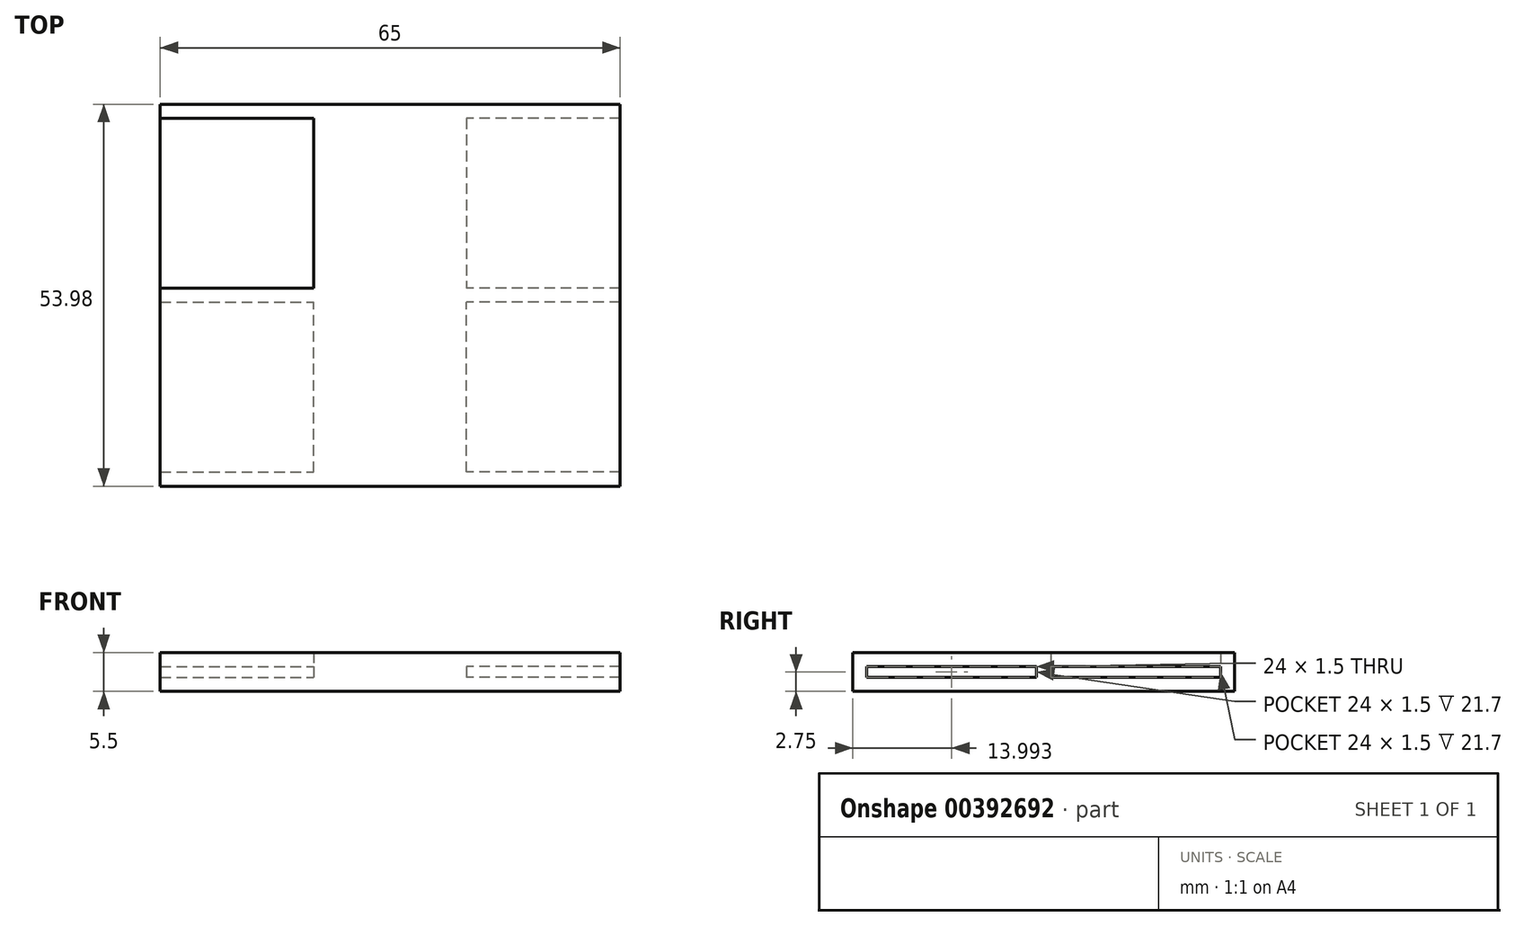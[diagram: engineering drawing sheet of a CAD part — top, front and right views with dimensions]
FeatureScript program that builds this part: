
annotation { "Feature Type Name" : "Feature", "Feature Type Description" : "" }
export const myFeature = defineFeature(function(context is Context, id is Id, definition is map)
    precondition{}
    {
        {
            assignVariable(context, id + "F0", {"name" : "SDThickness", "anyValue" : 1.5});
        }
        {
            var Q0;
            Q0=qCreatedBy(makeId("Top.planeOp"),FACE);
            var sketch = newSketch(context, id + "F1", { "sketchPlane" : qUnion([Q0])});
            skLineSegment(sketch, "E0.bottom", {"start": v(-42.8, 26.99) * mm, "end": v(42.8, 26.99) * mm});
            skLineSegment(sketch, "E0.top", {"start": v(-42.8, -26.99) * mm, "end": v(42.8, -26.99) * mm});
            skLineSegment(sketch, "E0.left", {"start": v(-42.8, 26.99) * mm, "end": v(-42.8, -26.99) * mm});
            skLineSegment(sketch, "E0.right", {"start": v(42.8, 26.99) * mm, "end": v(42.8, -26.99) * mm});
            skPoint(sketch, "E0.middle", {"position": v(0, 0) * mm});
            skSolve(sketch);
        }
        {
            var Q0;
            Q0=qCreatedBy(makeId("Top.planeOp"),FACE);
            var sketch = newSketch(context, id + "F2", { "sketchPlane" : qUnion([Q0])});
            skLineSegment(sketch, "E1.0", {"start": v(-42.8, 26.99) * mm, "end": v(42.8, 26.99) * mm});
            skLineSegment(sketch, "E2.0", {"start": v(-42.8, 26.99) * mm, "end": v(-42.8, -26.99) * mm});
            skLineSegment(sketch, "E3.0", {"start": v(-42.8, -26.99) * mm, "end": v(42.8, -26.99) * mm});
            skLineSegment(sketch, "E4.0", {"start": v(42.8, 26.99) * mm, "end": v(42.8, -26.99) * mm});
            skLineSegment(sketch, "E5.bottom", {"start": v(-42.8, 25) * mm, "end": v(-10.8, 25) * mm});
            skLineSegment(sketch, "E5.top", {"start": v(-42.8, 1) * mm, "end": v(-10.8, 1) * mm});
            skLineSegment(sketch, "E5.left", {"start": v(-42.8, 25) * mm, "end": v(-42.8, 1) * mm});
            skLineSegment(sketch, "E5.right", {"start": v(-10.8, 25) * mm, "end": v(-10.8, 1) * mm});
            skLineSegment(sketch, "E6.bottom", {"start": v(42.8, 25) * mm, "end": v(10.8, 25) * mm});
            skLineSegment(sketch, "E6.top", {"start": v(42.8, 1) * mm, "end": v(10.8, 1) * mm});
            skLineSegment(sketch, "E6.left", {"start": v(42.8, 25) * mm, "end": v(42.8, 1) * mm});
            skLineSegment(sketch, "E6.right", {"start": v(10.8, 25) * mm, "end": v(10.8, 1) * mm});
            skLineSegment(sketch, "E7.bottom", {"start": v(42.8, -25) * mm, "end": v(10.8, -25) * mm});
            skLineSegment(sketch, "E7.top", {"start": v(42.8, -1) * mm, "end": v(10.8, -1) * mm});
            skLineSegment(sketch, "E7.left", {"start": v(42.8, -25) * mm, "end": v(42.8, -1) * mm});
            skLineSegment(sketch, "E7.right", {"start": v(10.8, -25) * mm, "end": v(10.8, -1) * mm});
            skLineSegment(sketch, "E8.bottom", {"start": v(-42.8, -25) * mm, "end": v(-10.8, -25) * mm});
            skLineSegment(sketch, "E8.top", {"start": v(-42.8, -1) * mm, "end": v(-10.8, -1) * mm});
            skLineSegment(sketch, "E8.left", {"start": v(-42.8, -25) * mm, "end": v(-42.8, -1) * mm});
            skLineSegment(sketch, "E8.right", {"start": v(-10.8, -25) * mm, "end": v(-10.8, -1) * mm});
            skLineSegment(sketch, "E9", {"start": v(-26.8, 25) * mm, "end": v(-26.8, 26.99) * mm, "construction": true});
            skLineSegment(sketch, "E10", {"start": v(-26.8, 1) * mm, "end": v(-26.8, -1) * mm, "construction": true});
            skLineSegment(sketch, "E11", {"start": v(-26.8, -25) * mm, "end": v(-26.8, -26.99) * mm, "construction": true});
            skLineSegment(sketch, "E12", {"start": v(26.8, 25) * mm, "end": v(26.8, 26.99) * mm, "construction": true});
            skLineSegment(sketch, "E13", {"start": v(26.8, 1) * mm, "end": v(26.8, -1) * mm, "construction": true});
            skLineSegment(sketch, "E14", {"start": v(26.8, -25) * mm, "end": v(26.8, -26.99) * mm, "construction": true});
            skLineSegment(sketch, "E15", {"start": v(32.5, 27) * mm, "end": v(32.5, -26.99) * mm});
            skLineSegment(sketch, "E16", {"start": v(-32.5, 26.99) * mm, "end": v(-32.5, -26.99) * mm});
            skLineSegment(sketch, "E17", {"start": v(32.5, 27) * mm, "end": v(-32.5, -27) * mm, "construction": true});
            skLineSegment(sketch, "E18", {"start": v(-32.5, 27) * mm, "end": v(32.5, -27) * mm, "construction": true});
            skSolve(sketch);
        }
        {
            var Q0;
            {var subQ11=sQuery(id+"F2.wireOp",EDGE,"E5.right");Q0=makeQuery(id+"F2.imprint","IMPRINT",FACE,{"disambiguationData":[TD([[makeQuery(id+"F2.imprint","IMPRINT",EDGE,{"derivedFrom":subQ11}),1.0]])]});}
            var Q1;
            {var subQ0=sQuery(id+"F2.wireOp",EDGE,"E6.right");Q1=makeQuery(id+"F2.imprint","IMPRINT",FACE,{"disambiguationData":[TD([[makeQuery(id+"F2.imprint","IMPRINT",EDGE,{"derivedFrom":subQ0}),1.0]])]});}
            var Q2;
            {var subQ0=sQuery(id+"F2.wireOp",EDGE,"E8.right");Q2=makeQuery(id+"F2.imprint","IMPRINT",FACE,{"disambiguationData":[TD([[makeQuery(id+"F2.imprint","IMPRINT",EDGE,{"derivedFrom":subQ0}),1.0]])]});}
            var Q3;
            {var subQ0=sQuery(id+"F2.wireOp",EDGE,"E5.right");Q3=makeQuery(id+"F2.imprint","IMPRINT",FACE,{"disambiguationData":[TD([[makeQuery(id+"F2.imprint","IMPRINT",EDGE,{"derivedFrom":subQ0}),-1.0]])]});}
            var Q4;
            {var subQ0=sQuery(id+"F2.wireOp",EDGE,"E7.right");Q4=makeQuery(id+"F2.imprint","IMPRINT",FACE,{"disambiguationData":[TD([[makeQuery(id+"F2.imprint","IMPRINT",EDGE,{"derivedFrom":subQ0}),-1.0]])]});}
            extrude(context, id + "F3", {"entities" : qUnion([Q0, Q1, Q2, Q3, Q4]), "depth" : -2 * mm});
        }
        {
            var Q0;
            {var subQ11=sQuery(id+"F2.wireOp",EDGE,"E5.right");Q0=makeQuery(id+"F2.imprint","IMPRINT",FACE,{"disambiguationData":[TD([[makeQuery(id+"F2.imprint","IMPRINT",EDGE,{"derivedFrom":subQ11}),1.0]])]});}
            extrude(context, id + "F4", {"entities" : qUnion([Q0]), "operationType" : NewBodyOperationType.ADD, "depth" : (getVariable(context, 'SDThickness')) * mm});
        }
        {
            var Q0;
            Q0=makeQuery(id+"F4.opExtrude","CAP_FACE",FACE,{"disambiguationData":[OSD([sQuery(id+"F2.wireOp",EDGE,"E1.0"),sQuery(id+"F2.wireOp",EDGE,"E3.0"),sQuery(id+"F2.wireOp",EDGE,"E5.bottom"),sQuery(id+"F2.wireOp",EDGE,"E5.top"),sQuery(id+"F2.wireOp",EDGE,"E5.right"),sQuery(id+"F2.wireOp",EDGE,"E6.bottom"),sQuery(id+"F2.wireOp",EDGE,"E6.top"),sQuery(id+"F2.wireOp",EDGE,"E6.right"),sQuery(id+"F2.wireOp",EDGE,"E7.bottom"),sQuery(id+"F2.wireOp",EDGE,"E7.top"),sQuery(id+"F2.wireOp",EDGE,"E7.right"),sQuery(id+"F2.wireOp",EDGE,"E8.bottom"),sQuery(id+"F2.wireOp",EDGE,"E8.top"),sQuery(id+"F2.wireOp",EDGE,"E8.right"),sQuery(id+"F2.wireOp",EDGE,"E15"),sQuery(id+"F2.wireOp",EDGE,"E16")])],"isStart":false});
            var sketch = newSketch(context, id + "F5", { "sketchPlane" : qUnion([Q0])});
            skLineSegment(sketch, "E19.0.0", {"start": v(10.8, -1) * mm, "end": v(32.5, -1) * mm});
            skLineSegment(sketch, "E19.0.1", {"start": v(32.5, -1) * mm, "end": v(32.5, 1) * mm});
            skLineSegment(sketch, "E19.0.2", {"start": v(32.5, 1) * mm, "end": v(10.8, 1) * mm});
            skLineSegment(sketch, "E19.0.3", {"start": v(10.8, 1) * mm, "end": v(10.8, 25) * mm});
            skLineSegment(sketch, "E19.0.4", {"start": v(10.8, 25) * mm, "end": v(32.5, 25) * mm});
            skLineSegment(sketch, "E19.0.5", {"start": v(32.5, 25) * mm, "end": v(32.5, 26.99) * mm});
            skLineSegment(sketch, "E19.0.6", {"start": v(32.5, 26.99) * mm, "end": v(-32.5, 26.99) * mm});
            skLineSegment(sketch, "E19.0.7", {"start": v(-32.5, 26.99) * mm, "end": v(-32.5, 25) * mm});
            skLineSegment(sketch, "E19.0.8", {"start": v(-32.5, 25) * mm, "end": v(-10.8, 25) * mm});
            skLineSegment(sketch, "E19.0.9", {"start": v(-10.8, 25) * mm, "end": v(-10.8, 1) * mm});
            skLineSegment(sketch, "E19.0.10", {"start": v(-10.8, 1) * mm, "end": v(-32.5, 1) * mm});
            skLineSegment(sketch, "E19.0.11", {"start": v(-32.5, 1) * mm, "end": v(-32.5, -1) * mm});
            skLineSegment(sketch, "E19.0.12", {"start": v(-32.5, -1) * mm, "end": v(-10.8, -1) * mm});
            skLineSegment(sketch, "E19.0.13", {"start": v(-10.8, -1) * mm, "end": v(-10.8, -25) * mm});
            skLineSegment(sketch, "E19.0.14", {"start": v(-10.8, -25) * mm, "end": v(-32.5, -25) * mm});
            skLineSegment(sketch, "E19.0.15", {"start": v(-32.5, -25) * mm, "end": v(-32.5, -26.99) * mm});
            skLineSegment(sketch, "E19.0.16", {"start": v(-32.5, -26.99) * mm, "end": v(32.5, -26.99) * mm});
            skLineSegment(sketch, "E19.0.17", {"start": v(32.5, -26.99) * mm, "end": v(32.5, -25) * mm});
            skLineSegment(sketch, "E19.0.18", {"start": v(32.5, -25) * mm, "end": v(10.8, -25) * mm});
            skLineSegment(sketch, "E19.0.19", {"start": v(10.8, -25) * mm, "end": v(10.8, -1) * mm});
            skLineSegment(sketch, "E20.0.0", {"start": v(-10.8, 25) * mm, "end": v(-32.5, 25) * mm});
            skLineSegment(sketch, "E20.0.1", {"start": v(-32.5, 25) * mm, "end": v(-32.5, 1) * mm});
            skLineSegment(sketch, "E20.0.2", {"start": v(-32.5, 1) * mm, "end": v(-10.8, 1) * mm});
            skLineSegment(sketch, "E20.0.3", {"start": v(-10.8, 1) * mm, "end": v(-10.8, 25) * mm});
            skLineSegment(sketch, "E21.0.0", {"start": v(-32.5, -1) * mm, "end": v(-32.5, -25) * mm});
            skLineSegment(sketch, "E21.0.1", {"start": v(-32.5, -25) * mm, "end": v(-10.8, -25) * mm});
            skLineSegment(sketch, "E21.0.2", {"start": v(-10.8, -25) * mm, "end": v(-10.8, -1) * mm});
            skLineSegment(sketch, "E21.0.3", {"start": v(-10.8, -1) * mm, "end": v(-32.5, -1) * mm});
            skLineSegment(sketch, "E22.0.0", {"start": v(32.5, -25) * mm, "end": v(32.5, -1) * mm});
            skLineSegment(sketch, "E22.0.1", {"start": v(32.5, -1) * mm, "end": v(10.8, -1) * mm});
            skLineSegment(sketch, "E22.0.2", {"start": v(10.8, -1) * mm, "end": v(10.8, -25) * mm});
            skLineSegment(sketch, "E22.0.3", {"start": v(10.8, -25) * mm, "end": v(32.5, -25) * mm});
            skLineSegment(sketch, "E23.0.0", {"start": v(32.5, 1) * mm, "end": v(32.5, 25) * mm});
            skLineSegment(sketch, "E23.0.1", {"start": v(32.5, 25) * mm, "end": v(10.8, 25) * mm});
            skLineSegment(sketch, "E23.0.2", {"start": v(10.8, 25) * mm, "end": v(10.8, 1) * mm});
            skLineSegment(sketch, "E23.0.3", {"start": v(10.8, 1) * mm, "end": v(32.5, 1) * mm});
            skSolve(sketch);
        }
        {
            var Q0;
            Q0=makeQuery(id+"F5.imprint","IMPRINT",FACE,{"disambiguationData":[TD([[makeQuery(id+"F5.imprint","IMPRINT",EDGE,{"derivedFrom":sQuery(id+"F5.wireOp",EDGE,"E19.0.1")}),-1.0]])]});
            var Q1;
            Q1=makeQuery(id+"F5.imprint","IMPRINT",FACE,{"disambiguationData":[TD([[makeQuery(id+"F5.imprint","IMPRINT",EDGE,{"derivedFrom":sQuery(id+"F5.wireOp",EDGE,"E20.0.0")}),-1.0]])]});
            var Q2;
            Q2=makeQuery(id+"F5.imprint","IMPRINT",FACE,{"disambiguationData":[TD([[makeQuery(id+"F5.imprint","IMPRINT",EDGE,{"derivedFrom":sQuery(id+"F5.wireOp",EDGE,"E21.0.0")}),1.0]])]});
            var Q3;
            Q3=makeQuery(id+"F5.imprint","IMPRINT",FACE,{"disambiguationData":[TD([[makeQuery(id+"F5.imprint","IMPRINT",EDGE,{"derivedFrom":sQuery(id+"F5.wireOp",EDGE,"E23.0.0")}),1.0]])]});
            var Q4;
            Q4=makeQuery(id+"F5.imprint","IMPRINT",FACE,{"disambiguationData":[TD([[makeQuery(id+"F5.imprint","IMPRINT",EDGE,{"derivedFrom":sQuery(id+"F5.wireOp",EDGE,"E22.0.0")}),1.0]])]});
            extrude(context, id + "F6", {"entities" : qUnion([Q0, Q1, Q2, Q3, Q4]), "operationType" : NewBodyOperationType.ADD, "depth" : 2 * mm});
        }
    });
